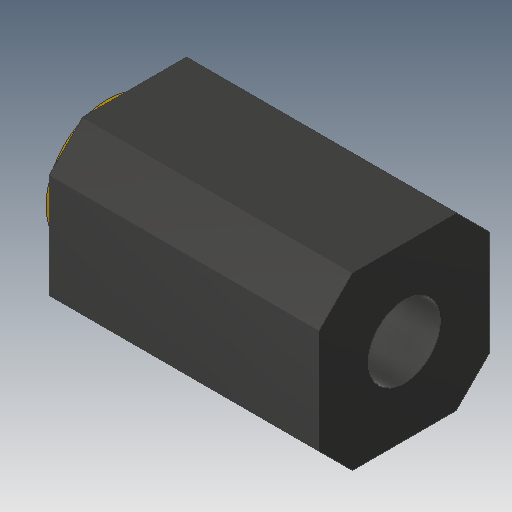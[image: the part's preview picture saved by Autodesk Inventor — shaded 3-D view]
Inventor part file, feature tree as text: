
AUTODESK INVENTOR PART (.ipt)
format: ipt  version: 2018 (Build 220112000, 112)  size: 129,536 bytes
history: native  units: mm
features: extrude x3, sketch x3, chamfer x1
ambient origin geometry x8: Origin, YZ Plane, XZ Plane, XY Plane, X Axis, Y Axis, Z Axis, Center Point
bodies: Solid1 (feature_tree), Solid2 (feature_tree)
feature tree (7):
  extrude  "Extrusion1"  Depth=2.54mm
  extrude  "Extrusion2"  Depth=4.0mm
  extrude  "Extrusion3"  Depth=4.0mm
  chamfer  "Chamfer1"  Distance=4.0mm
  sketch  "Sketch1"  dims[d0=2.54mm d1=2.54mm]
  sketch  "Sketch2"  dims[d2=4.0mm d3=0.0mm d4=1.83mm]
  sketch  "Sketch3"  dims[d5=0.4mm d6=0.0mm d7=1.07mm d8=4.0mm d9=0.0mm d10=0.5mm d11=2.0mm d12=45.0deg]
